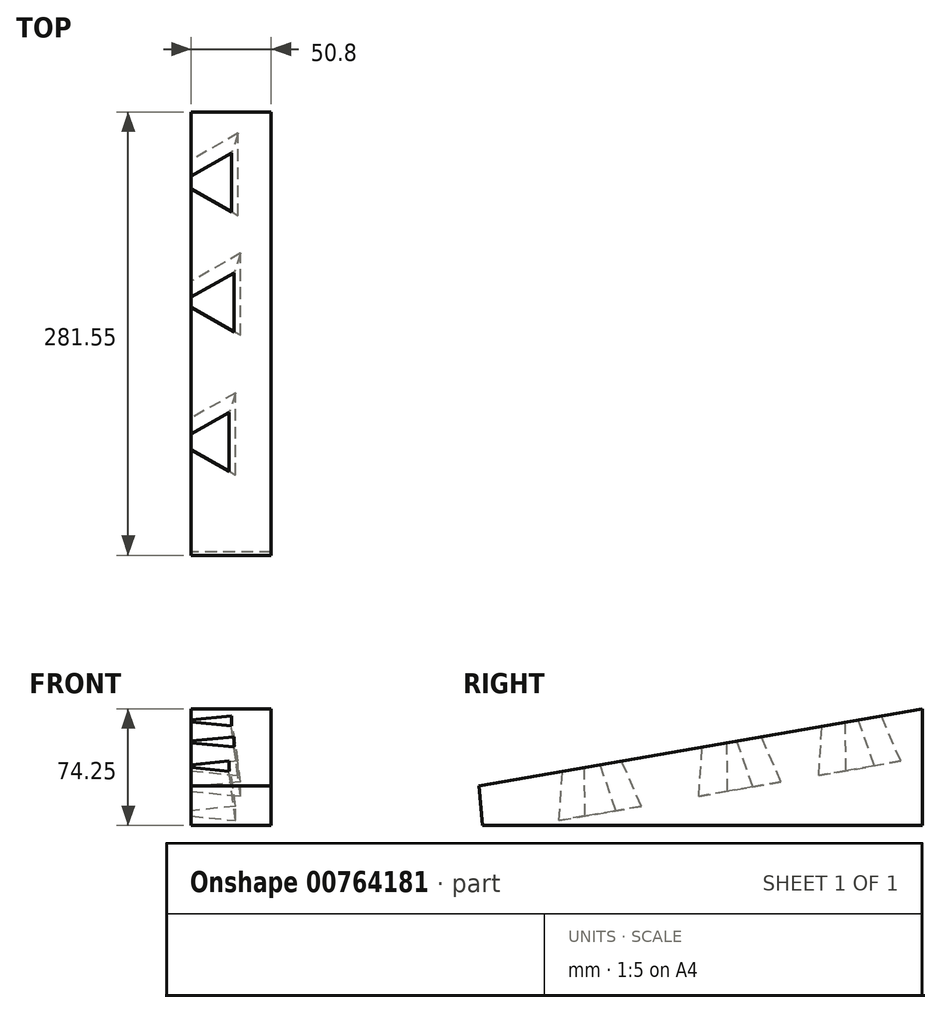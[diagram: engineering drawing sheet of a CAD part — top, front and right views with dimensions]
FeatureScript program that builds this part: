
annotation { "Feature Type Name" : "Feature", "Feature Type Description" : "" }
export const myFeature = defineFeature(function(context is Context, id is Id, definition is map)
    precondition{}
    {
        {
            var Q0;
            Q0=qCreatedBy(makeId("Right.planeOp"),FACE);
            var sketch = newSketch(context, id + "F0", { "sketchPlane" : qUnion([Q0])});
            skLineSegment(sketch, "E0", {"start": v(-132.21, -47.86) * mm, "end": v(147.19, -47.86) * mm});
            skLineSegment(sketch, "E1", {"start": v(147.19, -47.86) * mm, "end": v(147.19, 26.39) * mm});
            skLineSegment(sketch, "E2", {"start": v(147.19, 26.39) * mm, "end": v(-134.36, -22.55) * mm});
            skLineSegment(sketch, "E3", {"start": v(-134.36, -22.55) * mm, "end": v(-132.21, -47.86) * mm});
            skSolve(sketch);
        }
        {
            var Q0;
            Q0=makeQuery(id+"F0.imprint","IMPRINT",FACE,{"disambiguationData":[TD([[makeQuery(id+"F0.imprint","IMPRINT",EDGE,{"derivedFrom":sQuery(id+"F0.wireOp",EDGE,"E0")}),1.0]])]});
            extrude(context, id + "F1", {"entities" : qUnion([Q0]), "depth" : 50.8 * mm, "offsetDistance" : 25.4 * mm});
        }
        {
            var Q0;
            Q0=makeQuery(id+"F1.opExtrude","SWEPT_FACE",FACE,{"disambiguationData":[OSD([sQuery(id+"F0.wireOp",EDGE,"E2")])]});
            var sketch = newSketch(context, id + "F2", { "sketchPlane" : qUnion([Q0])});
            skLineSegment(sketch, "E4", {"start": v(0, 108.34) * mm, "end": v(25.5, 123.07) * mm});
            skLineSegment(sketch, "E5", {"start": v(25.5, 123.07) * mm, "end": v(25.5, 84.97) * mm});
            skLineSegment(sketch, "E6", {"start": v(25.5, 84.97) * mm, "end": v(0, 99.7) * mm});
            skLineSegment(sketch, "E7", {"start": v(0, 30.14) * mm, "end": v(27.15, 45.81) * mm});
            skLineSegment(sketch, "E8", {"start": v(27.15, 45.81) * mm, "end": v(27.15, 7.71) * mm});
            skLineSegment(sketch, "E9", {"start": v(27.15, 7.71) * mm, "end": v(0, 23.38) * mm});
            skLineSegment(sketch, "E10", {"start": v(0, -58.1) * mm, "end": v(23.97, -44.26) * mm});
            skLineSegment(sketch, "E11", {"start": v(23.97, -44.26) * mm, "end": v(23.97, -82.36) * mm});
            skLineSegment(sketch, "E12", {"start": v(23.97, -82.36) * mm, "end": v(0, -68.52) * mm});
            skSolve(sketch);
        }
        {
            var Q0;
            {var subQ0=sQuery(id+"F2.wireOp",EDGE,"E10");Q0=makeQuery(id+"F2.imprint","IMPRINT",FACE,{"disambiguationData":[TD([[makeQuery(id+"F2.imprint","IMPRINT",EDGE,{"derivedFrom":subQ0}),-1.0]])]});}
            var Q1;
            {var subQ0=sQuery(id+"F2.wireOp",EDGE,"E4");Q1=makeQuery(id+"F2.imprint","IMPRINT",FACE,{"disambiguationData":[TD([[makeQuery(id+"F2.imprint","IMPRINT",EDGE,{"derivedFrom":subQ0}),-1.0]])]});}
            var Q2;
            {var subQ0=sQuery(id+"F2.wireOp",EDGE,"E7");Q2=makeQuery(id+"F2.imprint","IMPRINT",FACE,{"disambiguationData":[TD([[makeQuery(id+"F2.imprint","IMPRINT",EDGE,{"derivedFrom":subQ0}),-1.0]])]});}
            var Q3;
            Q3=sQuery(id+"F2.wireOp",EDGE,"E7");
            extrude(context, id + "F3", {"entities" : qUnion([Q0, Q1, Q2]), "operationType" : NewBodyOperationType.REMOVE, "surfaceEntities" : qUnion([Q3]), "oppositeDirection" : true, "depth" : 30.48 * mm, "offsetDistance" : 25.4 * mm, "hasDraft" : true, "draftAngle" : 8 * degree});
        }
    });
